# Revit family: ledriga-p_re295-34_40w-ble2-830_840_542004095300_6de5
name_source: partatom
category: Lighting Fixtures
units: mm (PartAtom-declared; Revit-internal decimal feet)

## family parameters
Cut with Voids When Loaded = No
Host = Face
Light Source = No
Part Type = Normal
Room Calculation Point = No
Round Connector Dimension = Use Diameter
Shared = No

## types (1)
- LEDRiga-P Re295-34/40W-BLE2-830/840 (1 x LED, 52 lm, 3000)
    Apparent Load = 40 VA
    Approval mark = CE, ENEC
    CIE Flux Codes = 46 77 94 69 100
    Color Rendering = 80
    Color Temperature = 3000
    Control Gear = Electronic ballast
    Default Elevation = 1800 mm
    Description = Stylish direct/indirect suspended LED panel. Clean minimalistic design. Low Glare UGR19, suitable for office spaces. Flexible due to 3000/3500/4000K CCT and Power Switch.
    Frequency = 60 Hz
    Height = 16 mm
    Lamp = 1 x LED
    Lamp Light Flux = 52 lm
    Lamp count = 1
    Length = 1200 mm
    Luminous efficacy = 1 lm/W
    Manufacturer = OPPLE
    ModVariant = No
    Model = 542004095300
    Mounting Place = Ceiling
    Mounting Type = Pendant
    Number of Poles = 1
    OnlyDefault = Yes
    Power Factor = 1
    Product Name = LEDRiga-P Re295-34/40W-BLE2-830/840
    Product group = Pendant luminaire
    ProductGroupID = 9
    Protection Class = Protection class II
    Protection Degree = IP 20
    RLX_Detail_Level = 1
    RlxData = <blob elided: 159129 chars, md5=2294ede9>
    Socket = socket
    Standby Power = 0 W
    System Light Flux = 52 lm
    System Power = 40 W
    Type Comments = Product without accessories
    Type Image = web_riga.jpg
    URL = http://relux.com
    VarID = ---
    Voltage = 230 V
    Voltage Range = 220-240 V
    Weight = 0.00 kg
    Width = 300 mm

## geometry (parser evidence)
native form markers: Blend x4, Sweep x12
no freeform markers — native parametric forms only
